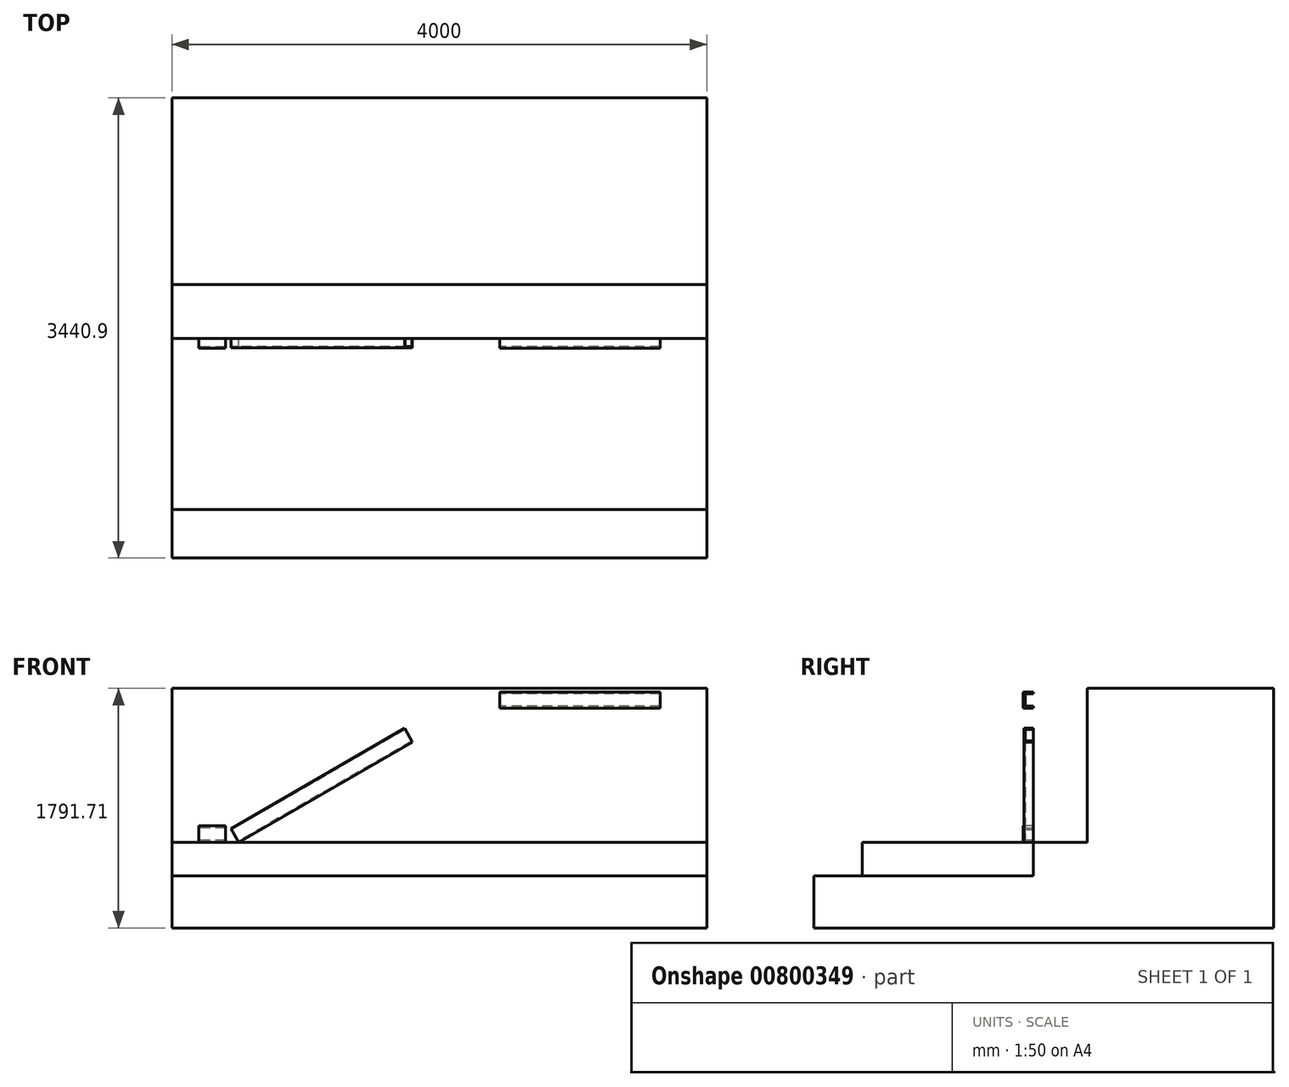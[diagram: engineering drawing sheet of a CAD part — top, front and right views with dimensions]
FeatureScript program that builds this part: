
annotation { "Feature Type Name" : "Feature", "Feature Type Description" : "" }
export const myFeature = defineFeature(function(context is Context, id is Id, definition is map)
    precondition{}
    {
        {
            var Q0;
            Q0=qCreatedBy(makeId("Front.planeOp"),FACE);
            var sketch = newSketch(context, id + "F0", { "sketchPlane" : qUnion([Q0])});
            skLineSegment(sketch, "E0", {"start": v(2000, 0) * mm, "end": v(-2000, 0) * mm});
            skLineSegment(sketch, "E1.0", {"start": v(2000, 1150) * mm, "end": v(-2000, 1150) * mm});
            skLineSegment(sketch, "E2", {"start": v(0, 0) * mm, "end": v(0, 1644.1) * mm, "construction": true});
            skLineSegment(sketch, "E3.0", {"start": v(2000, 0) * mm, "end": v(2000, 1644.1) * mm, "construction": true});
            skLineSegment(sketch, "E4.0", {"start": v(-2000, 0) * mm, "end": v(-2000, 1644.1) * mm, "construction": true});
            skSolve(sketch);
        }
        {
            var Q0;
            Q0=qCreatedBy(makeId("Right.planeOp"),FACE);
            cPlane(context, id + "F1", {"entities" : qUnion([Q0]), "cplaneType" : CPlaneType.OFFSET, "offset" : 2000 * mm, "width" : 150 * mm, "height" : 150 * mm});
        }
        {
            var Q0;
            Q0=qCreatedBy(id+"F1.planeOp",FACE);
            var sketch = newSketch(context, id + "F2", { "sketchPlane" : qUnion([Q0])});
            skLineSegment(sketch, "E5.bottom", {"start": v(0, 0) * mm, "end": v(-1280, 0) * mm});
            skLineSegment(sketch, "E5.top", {"start": v(0, -250) * mm, "end": v(-1280, -250) * mm});
            skLineSegment(sketch, "E5.left", {"start": v(0, 0) * mm, "end": v(0, -250) * mm});
            skLineSegment(sketch, "E5.right", {"start": v(-1280, 0) * mm, "end": v(-1280, -250) * mm});
            skSolve(sketch);
        }
        {
            var Q0;
            Q0 = qSketchRegion(id + "F2", true);
            extrude(context, id + "F3", {"entities" : qUnion([Q0]), "oppositeDirection" : true, "depth" : 4000 * mm, "offsetDistance" : 25 * mm});
        }
        {
            var Q0;
            Q0=makeQuery(id+"F3.opExtrude","CAP_FACE",FACE,{"disambiguationData":[OSD([sQuery(id+"F2.wireOp",EDGE,"E5.bottom"),sQuery(id+"F2.wireOp",EDGE,"E5.top"),sQuery(id+"F2.wireOp",EDGE,"E5.left"),sQuery(id+"F2.wireOp",EDGE,"E5.right")])],"isStart":true});
            var sketch = newSketch(context, id + "F4", { "sketchPlane" : qUnion([Q0])});
            skLineSegment(sketch, "E6", {"start": v(0, 0) * mm, "end": v(403.47, 0) * mm});
            skLineSegment(sketch, "E7", {"start": v(403.47, 0) * mm, "end": v(403.47, 1152.61) * mm});
            skLineSegment(sketch, "E8", {"start": v(403.47, 1152.61) * mm, "end": v(1798.15, 1152.61) * mm});
            skLineSegment(sketch, "E9", {"start": v(1798.15, 1152.61) * mm, "end": v(1798.15, -639.1) * mm});
            skLineSegment(sketch, "E10", {"start": v(1798.15, -639.1) * mm, "end": v(-1642.75, -639.1) * mm});
            skLineSegment(sketch, "E11", {"start": v(-1642.75, -639.1) * mm, "end": v(-1642.75, -250) * mm});
            skLineSegment(sketch, "E12", {"start": v(-1642.75, -250) * mm, "end": v(0, -250) * mm});
            skLineSegment(sketch, "E13", {"start": v(0, -250) * mm, "end": v(0, 0) * mm});
            skSolve(sketch);
        }
        {
            var Q0;
            Q0 = qSketchRegion(id + "F4", true);
            extrude(context, id + "F5", {"entities" : qUnion([Q0]), "oppositeDirection" : true, "depth" : 4000 * mm, "offsetDistance" : 25 * mm});
        }
        {
            var Q0;
            Q0=qCreatedBy(makeId("Right.planeOp"),FACE);
            cPlane(context, id + "F6", {"entities" : qUnion([Q0]), "cplaneType" : CPlaneType.OFFSET, "offset" : 1800 * mm, "oppositeDirection" : true, "width" : 150 * mm, "height" : 150 * mm});
        }
        {
            var Q0;
            Q0=qCreatedBy(id+"F6.planeOp",FACE);
            var sketch = newSketch(context, id + "F7", { "sketchPlane" : qUnion([Q0])});
            skLineSegment(sketch, "E14", {"start": v(-75, 0) * mm, "end": v(0, 0) * mm});
            skLineSegment(sketch, "E15", {"start": v(0, 0) * mm, "end": v(0, 17.45) * mm});
            skLineSegment(sketch, "E16", {"start": v(0, 17.45) * mm, "end": v(-63.32, 17.45) * mm});
            skLineSegment(sketch, "E17", {"start": v(-63.32, 17.45) * mm, "end": v(-63.32, 107.55) * mm});
            skLineSegment(sketch, "E18", {"start": v(-63.32, 107.55) * mm, "end": v(0, 107.55) * mm});
            skLineSegment(sketch, "E19", {"start": v(0, 107.55) * mm, "end": v(0, 125) * mm});
            skLineSegment(sketch, "E20", {"start": v(0, 125) * mm, "end": v(-75, 125) * mm});
            skLineSegment(sketch, "E21", {"start": v(-75, 125) * mm, "end": v(-75, 0) * mm});
            skSolve(sketch);
        }
        {
            var Q0;
            Q0 = qSketchRegion(id + "F7", true);
            extrude(context, id + "F8", {"entities" : qUnion([Q0]), "depth" : 200 * mm, "offsetDistance" : 25 * mm});
        }
        {
            var Q0;
            Q0=qCreatedBy(makeId("Front.planeOp"),FACE);
            var sketch = newSketch(context, id + "F9", { "sketchPlane" : qUnion([Q0])});
            skLineSegment(sketch, "E22", {"start": v(-1500, 0) * mm, "end": v(448.56, 1125) * mm});
            skLineSegment(sketch, "E23", {"start": v(-970.02, 1125) * mm, "end": v(2355.68, 1125) * mm, "construction": true});
            skLineSegment(sketch, "E24", {"start": v(448.56, 1125) * mm, "end": v(2355.68, 1125) * mm});
            skLineSegment(sketch, "E25", {"start": v(448.56, 1125) * mm, "end": v(448.56, 550.67) * mm});
            skLineSegment(sketch, "E26", {"start": v(-1500, 0) * mm, "end": v(-2210.22, 1230.14) * mm, "construction": true});
            skSolve(sketch);
        }
        {
            var Q0;
            Q0=qCreatedBy(makeId("Right.planeOp"),FACE);
            cPlane(context, id + "F10", {"entities" : qUnion([Q0]), "cplaneType" : CPlaneType.OFFSET, "offset" : 450 * mm, "width" : 150 * mm, "height" : 150 * mm});
        }
        {
            var Q0;
            Q0=qCreatedBy(id+"F10.planeOp",FACE);
            var sketch = newSketch(context, id + "F11", { "sketchPlane" : qUnion([Q0])});
            skLineSegment(sketch, "E27", {"start": v(0, 1005) * mm, "end": v(-75, 1005) * mm});
            skLineSegment(sketch, "E28", {"start": v(-75, 1005) * mm, "end": v(-75, 1125) * mm});
            skLineSegment(sketch, "E29", {"start": v(-75, 1125) * mm, "end": v(0, 1125) * mm});
            skLineSegment(sketch, "E30", {"start": v(0, 1125) * mm, "end": v(0, 1110.93) * mm});
            skLineSegment(sketch, "E31", {"start": v(0, 1110.93) * mm, "end": v(-62.07, 1110.93) * mm});
            skLineSegment(sketch, "E32", {"start": v(-62.07, 1110.93) * mm, "end": v(-62.07, 1019.07) * mm});
            skLineSegment(sketch, "E33", {"start": v(-62.07, 1019.07) * mm, "end": v(0, 1019.07) * mm});
            skLineSegment(sketch, "E34", {"start": v(0, 1019.07) * mm, "end": v(0, 1005) * mm});
            skSolve(sketch);
        }
        {
            var Q0;
            Q0 = qSketchRegion(id + "F11", true);
            extrude(context, id + "F12", {"entities" : qUnion([Q0]), "depth" : 1200 * mm, "offsetDistance" : 25 * mm});
        }
        {
            var Q0;
            Q0=qCreatedBy(makeId("Right.planeOp"),FACE);
            cPlane(context, id + "F13", {"entities" : qUnion([Q0]), "cplaneType" : CPlaneType.OFFSET, "offset" : 1500 * mm, "oppositeDirection" : true, "width" : 150 * mm, "height" : 150 * mm});
        }
        {
            var Q0;
            Q0=qCreatedBy(id+"F13.planeOp",FACE);
            var Q1;
            Q1=sQuery(id+"F9.wireOp",EDGE,"E26");
            cPlane(context, id + "F14", {"entities" : qUnion([Q0, Q1]), "cplaneType" : CPlaneType.LINE_ANGLE, "offset" : 25 * mm, "angle" : 0 * degree, "width" : 150 * mm, "height" : 150 * mm});
        }
        {
            var Q0;
            Q0=qCreatedBy(id+"F14.planeOp",FACE);
            var sketch = newSketch(context, id + "F15", { "sketchPlane" : qUnion([Q0])});
            skLineSegment(sketch, "E35", {"start": v(0, 870) * mm, "end": v(70, 870) * mm});
            skLineSegment(sketch, "E36", {"start": v(70, 870) * mm, "end": v(70, 750) * mm});
            skLineSegment(sketch, "E37", {"start": v(70, 750) * mm, "end": v(0, 750) * mm});
            skLineSegment(sketch, "E38", {"start": v(0, 750) * mm, "end": v(0, 760) * mm});
            skLineSegment(sketch, "E39", {"start": v(0, 760) * mm, "end": v(60, 760) * mm});
            skLineSegment(sketch, "E40", {"start": v(60, 760) * mm, "end": v(60, 860) * mm});
            skLineSegment(sketch, "E41", {"start": v(60, 860) * mm, "end": v(0, 860) * mm});
            skLineSegment(sketch, "E42", {"start": v(0, 860) * mm, "end": v(0, 870) * mm});
            skSolve(sketch);
        }
        {
            var Q0;
            Q0 = qSketchRegion(id + "F15", true);
            extrude(context, id + "F16", {"entities" : qUnion([Q0]), "oppositeDirection" : true, "depth" : 1500 * mm, "offsetDistance" : 25 * mm});
        }
    });
